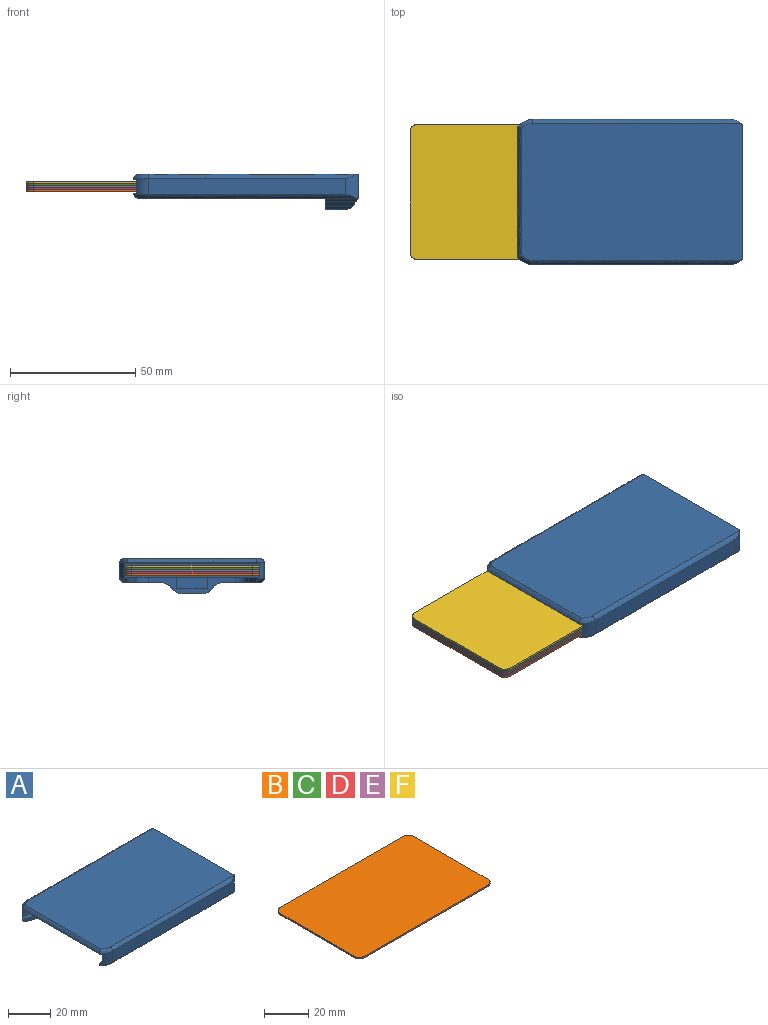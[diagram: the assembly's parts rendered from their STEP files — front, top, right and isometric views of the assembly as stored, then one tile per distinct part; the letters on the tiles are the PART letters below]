
ASSEMBLY  parts=6 mates=1
PART A: 49 faces, bbox 97x61.1x14.6 mm
  f0: plane 87.65x54.1mm, normal (0,0,1), area 1162mm2, adj f1,f4,f5,f14,f15,f16,f30,f31
  f1: plane 34.8x6.5mm, normal (-1,0,0), area 88.1mm2, adj f0,f2,f3,f31,f33,f36,f37,f38
  f2: plane 88.01x14.79mm, normal (0,0,-1), area 556.8mm2, adj f1,f8,f9,f25,f26,f30,f31,f35
  f3: plane 88.01x14.79mm, normal (0,0,-1), area 556.8mm2, adj f1,f7,f8,f27,f28,f32,f33,f34
  f4: cylinder r=7.5mm len=6.4mm, axis (0,0,-1), area 36.4mm2, adj f0,f10,f11,f13,f16,f21,f26,f35
  f5: cylinder r=7.5mm len=6.4mm, axis (0,0,-1), area 36.4mm2, adj f0,f11,f12,f13,f14,f24,f28,f34
  f6: plane 88.01x54.81mm, normal (0,0,1), area 4816.9mm2, adj f7,f8,f9,f20,f21,f22,f23,f24
  f7: cylinder r=7.25mm len=9.6mm, axis (0,0,-1), area 45.1mm2, adj f3,f6,f8,f12,f23,f27
  f8: plane 54x9.6mm, normal (1,0,0), area 518.4mm2, adj f2,f3,f6,f7,f9,f39
  f9: cylinder r=7.25mm len=9.6mm, axis (0,0,-1), area 45.1mm2, adj f2,f6,f8,f10,f20,f25
  f10: plane 78.6x6.4mm, normal (0,1,0), area 503mm2, adj f4,f9,f20,f25
  f11: plane 52x0.35mm, normal (-1,0,0), area 18.2mm2, adj f4,f5,f13,f22
  f12: plane 78.6x6.4mm, normal (0,-1,0), area 503mm2, adj f5,f7,f23,f27
  f13: plane 87.65x54.1mm, normal (0,0,-1), area 4740.3mm2, adj f4,f5,f11,f14,f15,f16,f18,f19
  f14: plane 86.69x5.7mm, normal (0,1,0), area 494.2mm2, adj f0,f5,f13,f15
  f15: plane 54.1x5.7mm, normal (-1,0,0), area 308.4mm2, adj f0,f13,f14,f16
  f16: plane 86.69x5.7mm, normal (0,-1,0), area 477mm2, adj f0,f4,f13,f15,f17,f19,f29
  f17: plane 3.02x0.25mm, normal (0,0,-1), area 0.6mm2, adj f16,f18,f19,f29
  f18: plane 5.67x2.05mm, normal (0,-1,0), area 11.5mm2, adj f13,f17,f19,f29
  f19: plane 5.68x1.03mm, normal (0.24,-0.97,0), area 5.8mm2, adj f13,f16,f17,f18
  f20: bspline ~96.55x1.6mm, area 189.4mm2, adj f6,f9,f10,f21
  f21: bspline ~6.39x4.41mm, area 14.1mm2, adj f4,f6,f20,f22
  f22: bspline ~60.66x1.6mm, area 120.5mm2, adj f6,f11,f21,f24
  f23: bspline ~96.55x1.6mm, area 189.4mm2, adj f6,f7,f12,f24
  f24: bspline ~6.39x4.41mm, area 14.1mm2, adj f5,f6,f22,f23
  f25: bspline ~96.55x1.6mm, area 189.4mm2, adj f2,f9,f10,f26
  f26: bspline ~6.39x4.41mm, area 14.1mm2, adj f2,f4,f25,f35
  f27: bspline ~96.55x1.6mm, area 189.4mm2, adj f3,f7,f12,f28
  f28: bspline ~6.39x4.41mm, area 14.1mm2, adj f3,f5,f27,f34
  f29: plane 5.66x0.25mm, normal (-1,0,0), area 1.4mm2, adj f13,f16,f17,f18
  f30: plane 61.49x1.95mm, normal (0,-1,0), area 119.9mm2, adj f0,f2,f31,f35
  f31: cylinder r=5mm len=5mm, axis (0,0,-1), area 15.3mm2, adj f0,f1,f2,f30
  f32: plane 61.49x1.95mm, normal (0,1,0), area 119.9mm2, adj f0,f3,f33,f34
  f33: cylinder r=5mm len=5mm, axis (0,0,-1), area 15.3mm2, adj f0,f1,f3,f32
  f34: plane 10.57x4.06mm, normal (-0.34,0.94,0), area 20mm2, adj f0,f3,f5,f28,f32
  f35: plane 10.57x4.06mm, normal (-0.34,-0.94,0), area 20mm2, adj f0,f2,f4,f26,f30
  f36: plane 7.86x7.31mm, normal (0,0,-1), area 57.4mm2, adj f1,f40,f41,f42
  f37: plane 12.07x1.65mm, normal (0,-0.71,-0.71), area 26.3mm2, adj f1,f39,f41,f42,f44
  f38: plane 12.07x1.65mm, normal (0,0.71,-0.71), area 26.3mm2, adj f1,f39,f40,f42,f43
  f39: plane 25.71x2.77mm, normal (0.83,0,-0.55), area 53.1mm2, adj f8,f37,f38,f42,f43,f44
  f40: cylinder r=5mm len=10.84mm, axis (1,0,0), area 35.6mm2, adj f1,f36,f38,f42
  f41: cylinder r=5mm len=10.84mm, axis (1,0,0), area 35.6mm2, adj f1,f36,f37,f42
  f42: cylinder r=5mm len=16.5mm, axis (0,-1,0), area 60.6mm2, adj f36,f37,f38,f39,f40,f41
  f43: cylinder r=5mm len=13mm, axis (1,0,0), area 49.2mm2, adj f1,f2,f38,f39
  f44: cylinder r=5mm len=13mm, axis (1,0,0), area 49.2mm2, adj f1,f3,f37,f39
  f45: plane 12.1x4.55mm, normal (-1,0,0), area 55.1mm2, adj f0,f46,f47,f48
  f46: plane 10.05x4.55mm, normal (0,1,0), area 45.7mm2, adj f0,f1,f45,f48
  f47: plane 10.05x4.55mm, normal (0,-1,0), area 45.7mm2, adj f0,f1,f45,f48
  f48: plane 12.1x10.05mm, normal (0,0,1), area 121.6mm2, adj f1,f45,f46,f47
PART B: 10 faces, bbox 85.6x54x0.8 mm
  f0: plane 48x0.8mm, normal (1,0,0), area 38.4mm2, adj f1,f7,f8,f9
  f1: cylinder r=3mm len=3mm, axis (0,0,-1), area 3.8mm2, adj f0,f2,f8,f9
  f2: plane 79.6x0.8mm, normal (0,1,0), area 63.7mm2, adj f1,f3,f8,f9
  f3: cylinder r=3mm len=3mm, axis (0,0,-1), area 3.8mm2, adj f2,f4,f8,f9
  f4: plane 48x0.8mm, normal (-1,0,0), area 38.4mm2, adj f3,f5,f8,f9
  f5: cylinder r=3mm len=3mm, axis (0,0,-1), area 3.8mm2, adj f4,f6,f8,f9
  f6: plane 79.6x0.8mm, normal (0,-1,0), area 63.7mm2, adj f5,f7,f8,f9
  f7: cylinder r=3mm len=3mm, axis (0,0,-1), area 3.8mm2, adj f0,f6,f8,f9
  f8: plane 85.6x54mm, normal (0,0,1), area 4614.7mm2, adj f0,f1,f2,f3,f4,f5,f6,f7
  f9: plane 85.6x54mm, normal (0,0,-1), area 4614.7mm2, adj f0,f1,f2,f3,f4,f5,f6,f7
PART C: same geometry as B
PART D: same geometry as B
PART E: same geometry as B
PART F: same geometry as B
PLACE A rot(axis=(1,0,0),0deg) t=(231.45,53.8,-53.42)mm
PLACE B rot(axis=(0,-1,0),180deg) t=(271.97,53.8,-51.82)mm
PLACE C rot(axis=(0,-1,0),180deg) t=(271.97,53.8,-49.42)mm
PLACE D rot(axis=(0,-1,0),180deg) t=(271.97,53.8,-51.02)mm
PLACE E rot(axis=(0,-1,0),180deg) t=(271.97,53.8,-50.22)mm
PLACE F rot(axis=(0,-1,0),180deg) t=(271.97,53.8,-48.62)mm
MATE slider B.f0 <-> A.f15  axis (-1,0,0) through (186.37,26.8,-52.22)mm
